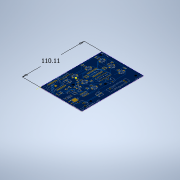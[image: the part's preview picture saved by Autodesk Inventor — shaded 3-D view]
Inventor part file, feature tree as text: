
AUTODESK INVENTOR PART (.ipt)
format: ipt  version: 2020 (Build 240168000, 168)  size: 342,016 bytes
history: native  units: in
note: dims shown in document units (in); Inventor stores cm internally (conversion verified against a paired STEP export)
features: other x2, sketch x2, extrude x1
ambient origin geometry x8: Origin, YZ Plane, XZ Plane, XY Plane, X Axis, Y Axis, Z Axis, Center Point
bodies: Solid1 (feature_tree)
feature tree (5):
  extrude  "Extrusion1"  Depth=2.9449in
  other  "Decal1"
  sketch  "Sketch1"  dims[d0=4.335in d1=2.9449in]
  sketch  "Sketch2"  dims[d2=0.0394in d3=0.0in d6=4.335in]
  other  "Image1"
